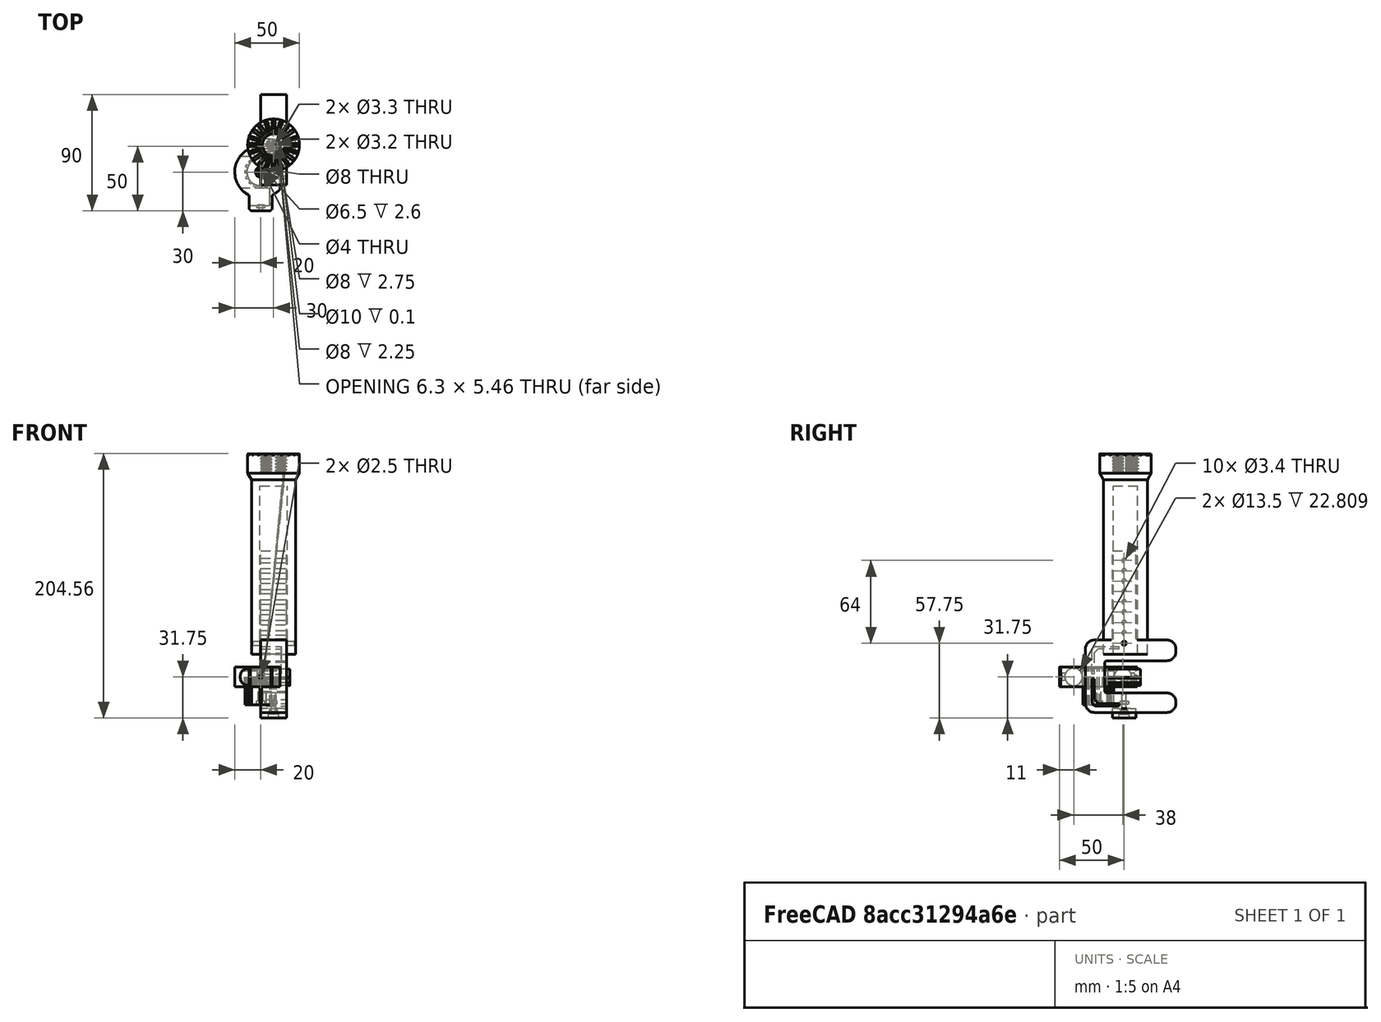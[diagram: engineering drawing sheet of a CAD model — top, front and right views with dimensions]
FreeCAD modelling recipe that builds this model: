
FCSTD DOCUMENT  (FreeCAD 0.18R4 (GitTag))
Label: sop_mic_2
License: All rights reserved
LicenseURL: http://en.wikipedia.org/wiki/All_rights_reserved
objects: Part::Cylinder×59, Part::Cut×55, Part::Box×30, Part::MultiFuse×23, Part::Fillet×12, Part::Prism×8, Mesh::Feature×7, Part::FeaturePython×7, Part::Chamfer×2, Part::Feature×2, App::DocumentObjectGroup×2, Part::Cone×1, Sketcher::SketchObject×1, PartDesign::Pad×1, PartDesign::Body×1, App::FeaturePython×1
note: 203 computed .brp shape members not serialized (recipe doc carries the construction recipe); baked Part::Feature solids carry a one-line shape summary decoded from their .brp

FEATURE [Part::Box] Box  label="Cube"
  AttacherType = Attacher::AttachEngine3D
  Height = 5
  Length = 20
  Width = 30
FEATURE [Part::Cylinder] Cylinder
  Angle = 360
  AttacherType = Attacher::AttachEngine3D
  Height = 10
  Placement = pos=(10,20,-2) rot=(0,0,1;0rad)
  Radius = 1.6
FEATURE [Part::Cut] Cut
  Base = -> Box
  Refine = true
  Tool = -> Cylinder
FEATURE [Part::Prism] Prism
  AttacherType = Attacher::AttachEngine3D
  Circumradius = 3.25
  Height = 10
  Placement = pos=(10,20,9) rot=(1,0,0;3.14159rad)
  Polygon = 6
FEATURE [Part::Cut] Cut001
  Base = -> Cut
  Refine = true
  Tool = -> Prism
FEATURE [Part::Box] Box001  label="Cube001"
  AttacherType = Attacher::AttachEngine3D
  Height = 40
  Length = 20
  Width = 5
FEATURE [Part::Box] Box002  label="Cube002"
  AttacherType = Attacher::AttachEngine3D
  Height = 5
  Length = 20
  Placement = pos=(0,0,35) rot=(0,0,1;0rad)
  Width = 40
FEATURE [Part::Prism] Prism002
  AttacherType = Attacher::AttachEngine3D
  Circumradius = 3.15
  Height = 2.5
  Placement = pos=(0,29,22.5) rot=(1,0,0;1.5708rad)
  Polygon = 6
FEATURE [Part::Cylinder] Cylinder016  label="Cylinder015"
  Angle = 360
  AttacherType = Attacher::AttachEngine3D
  Height = 7.25
  Placement = pos=(0,0,17.5) rot=(1,0,0;1.5708rad)
  Radius = 4
FEATURE [Part::Cylinder] Cylinder013  label="Cylinder012"
  Angle = 360
  AttacherType = Attacher::AttachEngine3D
  Height = 50
  Placement = pos=(0,-16,22.5) rot=(1,0,0;1.5708rad)
  Radius = 1.25
FEATURE [Part::Box] Box004  label="Cube004"
  AttacherType = Attacher::AttachEngine3D
  Height = 10
  Length = 20
  Placement = pos=(-10,0,12.5) rot=(0,0,1;0rad)
  Width = 7.25
FEATURE [Part::Cylinder] Cylinder015  label="Cylinder014"
  Angle = 360
  AttacherType = Attacher::AttachEngine3D
  Height = 7.25
  Placement = pos=(0,0,17.5) rot=(1,0,0;1.5708rad)
  Radius = 9
FEATURE [Part::Cut] Cut013
  Base = -> Cylinder015
  Placement = pos=(0,7.25,0) rot=(0,0,1;0rad)
  Refine = true
  Tool = -> Cylinder016
FEATURE [Part::Cylinder] Cylinder014  label="Cylinder013"
  Angle = 360
  AttacherType = Attacher::AttachEngine3D
  Height = 10
  Placement = pos=(0,-16,22.5) rot=(1,0,0;1.5708rad)
  Radius = 4
FEATURE [Part::MultiFuse] Fusion004
  Placement = pos=(0,57,0) rot=(0,0,1;0rad)
  Refine = true
  Shapes = -> [Cylinder013,Cylinder014]
FEATURE [Part::MultiFuse] Fusion005
  Placement = pos=(0,-26.5,-5) rot=(0,0,1;0rad)
  Refine = true
  Shapes = -> [Prism002,Fusion004]
FEATURE [Part::Cut] Cut012
  Base = -> Box004
  Refine = true
  Tool = -> Fusion005
FEATURE [Part::Fillet] Fillet004
  Base = -> Cut012
  Edges = 1 edges r=3: [Edge15]
FEATURE [Part::Fillet] Fillet005
  Base = -> Fillet004
  Edges = 3 edges r=3: [Edge13,Edge17,Edge20]
FEATURE [Part::MultiFuse] Fusion006
  Refine = true
  Shapes = -> [Cut013,Fillet005]
FEATURE [Part::Fillet] Fillet006  label="tornillos_para_metal"
  Base = -> Fusion006
  Edges = 4 edges r=1: [Edge5,Edge9,Edge12,Edge17]
  Placement = pos=(10,2.5,-2) rot=(-1,0,0;1.5708rad)
FEATURE [Part::Cylinder] Cylinder017  label="Cylinder016"
  Angle = 360
  AttacherType = Attacher::AttachEngine3D
  Height = 7
  Placement = pos=(10,0,-27) rot=(0,0,1;0rad)
  Radius = 12.5
FEATURE [Part::Prism] Prism003
  AttacherType = Attacher::AttachEngine3D
  Circumradius = 3.15
  Height = 3
  Placement = pos=(10,-4e-15,-20) rot=(1,0,0;3.14159rad)
  Polygon = 6
FEATURE [Part::Cut] Cut014
  Base = -> Cylinder017
  Refine = true
  Tool = -> Prism003
FEATURE [Part::Cylinder] Cylinder018  label="Cylinder017"
  Angle = 360
  AttacherType = Attacher::AttachEngine3D
  Height = 2.75
  Placement = pos=(10,0,-27) rot=(0,0,1;0rad)
  Radius = 4
FEATURE [Part::Cut] Cut015
  Base = -> Cut014
  Refine = true
  Tool = -> Cylinder018
FEATURE [Part::Cylinder] Cylinder019  label="Cylinder018"
  Angle = 360
  AttacherType = Attacher::AttachEngine3D
  Height = 22.75
  Placement = pos=(10,0,-31) rot=(0,0,1;0rad)
  Radius = 1.6
FEATURE [Part::Cut] Cut016  label="plato_tornillo"
  Base = -> Cut015
  Placement = pos=(0,20,42) rot=(0,0,1;0rad)
  Refine = true
  Tool = -> Cylinder019
FEATURE [Part::MultiFuse] Fusion
  Refine = true
  Shapes = -> [Cut001,Box001,Box002]
FEATURE [Part::Fillet] Fillet
  Base = -> Fusion
  Edges = 4 edges r=2: [Edge6,Edge14,Edge18,Edge33]
FEATURE [Part::Fillet] Fillet007  label="soporte_escritorio1"
  Base = -> Fillet
  Edges = 1 edges r=2: [Edge50]
FEATURE [Part::Box] Box005  label="Cube005"
  AttacherType = Attacher::AttachEngine3D
  Height = 80
  Length = 20
  Placement = pos=(0,11,40) rot=(0,0,1;0rad)
  Width = 18
FEATURE [Part::MultiFuse] Fusion007  label="soporte_escritorio2"
  Refine = true
  Shapes = -> [Fillet007,Box005]
FEATURE [Part::Cylinder] Cylinder021  label="Cylinder020"
  Angle = 360
  AttacherType = Attacher::AttachEngine3D
  Height = 140
  Placement = pos=(10,21,40) rot=(0,0,1;0rad)
  Radius = 17
FEATURE [Part::Box] Box006  label="Cube006"
  AttacherType = Attacher::AttachEngine3D
  Height = 130
  Length = 21
  Placement = pos=(-0.5,11.5,40) rot=(0,0,1;0rad)
  Width = 19
FEATURE [Part::Cut] Cut017  label="intermedio1"
  Base = -> Cylinder021
  Refine = true
  Tool = -> Box006
FEATURE [Part::Cylinder] Cylinder022  label="tornillo001"
  Angle = 360
  AttacherType = Attacher::AttachEngine3D
  Height = 50
  Placement = pos=(-16,20,48.5) rot=(0,1,0;1.5708rad)
  Radius = 1.7
FEATURE [Part::Cylinder] Cylinder023  label="tornillo002"
  Angle = 360
  AttacherType = Attacher::AttachEngine3D
  Height = 50
  Placement = pos=(-16,20,48.5) rot=(0,1,0;1.5708rad)
  Radius = 1.7
FEATURE [Part::Cut] Cut018  label="intermedio_partial"
  Base = -> Cut017
  Refine = true
  Tool = -> Cylinder022
FEATURE [Part::Cylinder] Cylinder024  label="tornillo003"
  Angle = 360
  AttacherType = Attacher::AttachEngine3D
  Height = 50
  Placement = pos=(-16,20,56.5) rot=(0,1,0;1.5708rad)
  Radius = 1.7
FEATURE [Part::Cylinder] Cylinder025  label="tornillo004"
  Angle = 360
  AttacherType = Attacher::AttachEngine3D
  Height = 50
  Placement = pos=(-16,20,64.5) rot=(0,1,0;1.5708rad)
  Radius = 1.7
FEATURE [Part::Cylinder] Cylinder026  label="tornillo005"
  Angle = 360
  AttacherType = Attacher::AttachEngine3D
  Height = 50
  Placement = pos=(-16,20,72.5) rot=(0,1,0;1.5708rad)
  Radius = 1.7
FEATURE [Part::Cylinder] Cylinder027  label="tornillo006"
  Angle = 360
  AttacherType = Attacher::AttachEngine3D
  Height = 50
  Placement = pos=(-16,20,80.5) rot=(0,1,0;1.5708rad)
  Radius = 1.7
FEATURE [Part::Cylinder] Cylinder028  label="tornillo007"
  Angle = 360
  AttacherType = Attacher::AttachEngine3D
  Height = 50
  Placement = pos=(-16,20,88.5) rot=(0,1,0;1.5708rad)
  Radius = 1.7
FEATURE [Part::Cylinder] Cylinder029  label="tornillo008"
  Angle = 360
  AttacherType = Attacher::AttachEngine3D
  Height = 50
  Placement = pos=(-16,20,96.5) rot=(0,1,0;1.5708rad)
  Radius = 1.7
FEATURE [Part::Cylinder] Cylinder030  label="tornillo009"
  Angle = 360
  AttacherType = Attacher::AttachEngine3D
  Height = 50
  Placement = pos=(-16,20,104.5) rot=(0,1,0;1.5708rad)
  Radius = 1.7
FEATURE [Part::Cylinder] Cylinder031  label="tornillo010"
  Angle = 360
  AttacherType = Attacher::AttachEngine3D
  Height = 50
  Placement = pos=(-16,20,112.5) rot=(0,1,0;1.5708rad)
  Radius = 1.7
FEATURE [Part::MultiFuse] Fusion008
  Refine = true
  Shapes = -> [Cylinder023,Cylinder024,Cylinder025,Cylinder026,Cylinder027,Cylinder028,Cylinder029,Cylinder031,Cylinder030]
FEATURE [Part::Cut] Cut019  label="soporte_escritorio_v2"
  Base = -> Fusion007
  Refine = true
  Tool = -> Fusion008
FEATURE [Mesh::Feature] Mesh  label="tornillos_para_metal (Meshed)"
FEATURE [Mesh::Feature] Mesh001  label="plato_tornillo_gordo_old (Meshed)"
FEATURE [Part::Cylinder] Cylinder032
  Angle = 360
  AttacherType = Attacher::AttachEngine3D
  Height = 10
  Placement = pos=(10,20,-2) rot=(0,0,1;0rad)
  Radius = 1.6
FEATURE [Part::Cylinder] Cylinder033
  Angle = 360
  AttacherType = Attacher::AttachEngine3D
  Height = 1.2
  Placement = pos=(10,20,-2) rot=(0,0,1;0rad)
  Radius = 5
FEATURE [Part::Cut] Cut020
  Base = -> Cylinder033
  Placement = pos=(0,0,5.8) rot=(0,0,1;0rad)
  Refine = true
  Tool = -> Cylinder032
FEATURE [Part::MultiFuse] Fusion009  label="soporte_escritorio_x"
  Refine = true
  Shapes = -> [Cut019,Cut020]
FEATURE [Part::Prism] Prism005
  AttacherType = Attacher::AttachEngine3D
  Circumradius = 3.25
  Height = 10
  Placement = pos=(10,20,12) rot=(1,0,0;3.14159rad)
  Polygon = 6
FEATURE [Part::Cut] Cut021
  Base = -> Fusion009
  Refine = true
  Tool = -> Prism005
FEATURE [Part::Cylinder] Cylinder034
  Angle = 360
  AttacherType = Attacher::AttachEngine3D
  Height = 1.5
  Placement = pos=(10,20,0) rot=(0,0,1;0rad)
  Radius = 4.6
FEATURE [Part::Cylinder] Cylinder035
  Angle = 360
  AttacherType = Attacher::AttachEngine3D
  Height = 10
  Placement = pos=(10,20,-2) rot=(0,0,1;0rad)
  Radius = 1.6
FEATURE [Part::Cut] Cut022
  Base = -> Cylinder034
  Refine = true
  Tool = -> Cylinder035
FEATURE [Part::MultiFuse] Fusion010  label="soporte_escritorio_y"
  Refine = true
  Shapes = -> [Cut022,Cut021]
FEATURE [Part::Prism] Prism006
  AttacherType = Attacher::AttachEngine3D
  Circumradius = 3.25
  Height = 2.3
  Placement = pos=(10,20,-28) rot=(1,0,0;3.14159rad)
  Polygon = 6
FEATURE [Part::Box] Box007  label="Cube007"
  AttacherType = Attacher::AttachEngine3D
  Height = 2.3
  Length = 6.5
  Placement = pos=(6.75,17.18,-30.3) rot=(0,0,1;0rad)
  Width = 2.82
FEATURE [Part::MultiFuse] Fusion011
  Placement = pos=(30,10,31.8) rot=(0,0,1;1.5708rad)
  Refine = true
  Shapes = -> [Prism006,Box007]
FEATURE [Part::Cylinder] Cylinder038
  Angle = 360
  AttacherType = Attacher::AttachEngine3D
  Height = 5
  Placement = pos=(10,20,0) rot=(0,0,1;0rad)
  Radius = 4.6
FEATURE [Part::Cylinder] Cylinder039
  Angle = 360
  AttacherType = Attacher::AttachEngine3D
  Height = 10
  Placement = pos=(10,20,-2) rot=(0,0,1;0rad)
  Radius = 1.6
FEATURE [Part::Cut] Cut025
  Base = -> Cylinder038
  Refine = true
  Tool = -> Cylinder039
FEATURE [Part::MultiFuse] Fusion012
  Refine = true
  Shapes = -> [Cut025,Fusion010]
FEATURE [Part::Cut] Cut026  label="soporte_escritorio"
  Base = -> Fusion012
  Refine = true
  Tool = -> Fusion011
FEATURE [Part::Cylinder] Cylinder003
  Angle = 360
  AttacherType = Attacher::AttachEngine3D
  Height = 23
  Radius = 11
FEATURE [Part::Box] Box009  label="Cube009"
  AttacherType = Attacher::AttachEngine3D
  Height = 5
  Length = 25
  Placement = pos=(14,-5,0) rot=(0,0,1;0rad)
  Width = 10
FEATURE [Part::Cylinder] Cylinder042
  Angle = 360
  AttacherType = Attacher::AttachEngine3D
  Height = 22
  Placement = pos=(0,0,15) rot=(0,1,0;1.5708rad)
  Radius = 1.1
FEATURE [Part::FeaturePython] Array  # Draft array (typed FeaturePython)
  Angle = 360
  ArrayType = 1
  Axis = (0,0,1)
  Base = -> Cylinder042
  Center = (0,0,0)
  Fuse = false
  IntervalAxis = (0,0,0)
  IntervalX = (1,0,0)
  IntervalY = (0,1,0)
  IntervalZ = (0,0,1)
  NumberPolar = 10
  NumberX = 2
  NumberY = 2
  NumberZ = 1
FEATURE [Part::Cut] Cut029
  Base = -> Array
  Refine = true
  Tool = -> Cylinder003
FEATURE [Part::Cylinder] Cylinder043
  Angle = 360
  AttacherType = Attacher::AttachEngine3D
  Height = 15
  Radius = 20
FEATURE [Part::FeaturePython] ScrewTap  label="M20x40.0-ScrewTap"  # Fasteners workbench fastener (typed FeaturePython)
  Placement = pos=(0,0,15) rot=(0,0,1;0rad)
  baseObject = -> Cylinder043 [Edge1]
  diameter = 14
  invert = false
  length = 40
  matchOuter = false
  offset = 0
  thread = true
FEATURE [Part::Cut] Cut028
  Base = -> Cylinder043
  Refine = true
  Tool = -> ScrewTap
FEATURE [Part::Cut] Cut003
  Base = -> Cut028
  Refine = true
  Tool = -> Cut029
FEATURE [Part::Box] Box010  label="Cube010"
  AttacherType = Attacher::AttachEngine3D
  Height = 5
  Length = 25
  Placement = pos=(-38,-5,0) rot=(0,0,1;0rad)
  Width = 10
FEATURE [Part::MultiFuse] Fusion014
  Refine = true
  Shapes = -> [Box010,Box009,Cut003]
FEATURE [Part::Fillet] Fillet008
  Base = -> Fusion014
  Edges = 7 edges r=3: [Edge6,Edge9,Edge11,Edge42,Edge43,Edge46,Edge47]
FEATURE [Part::Fillet] Fillet001
  Base = -> Fillet008
  Edges = 1 edges r=2: [Edge24]
FEATURE [Part::Fillet] Fillet002  label="final_part_soporte_superior_estante"
  Base = -> Fillet001
  Edges = 3 edges r=2: [Edge27,Edge71,Edge74]
FEATURE [Part::Cylinder] Cylinder044
  Angle = 360
  AttacherType = Attacher::AttachEngine3D
  Height = 20
  Radius = 40
FEATURE [Part::Cylinder] Cylinder045
  Angle = 360
  AttacherType = Attacher::AttachEngine3D
  Height = 20
  Radius = 20
FEATURE [Part::Cut] Cut030
  Base = -> Cylinder044
  Refine = true
  Tool = -> Cylinder045
FEATURE [Part::Cut] Cut031
  Base = -> Fillet002
  Refine = true
  Tool = -> Cut030
FEATURE [Part::Cylinder] Cylinder046
  Angle = 360
  AttacherType = Attacher::AttachEngine3D
  Height = 22
  Placement = pos=(0,0,15) rot=(0,1,0;1.5708rad)
  Radius = 1.1
FEATURE [Part::FeaturePython] Array001  # Draft array (typed FeaturePython)
  Angle = 360
  ArrayType = 1
  Axis = (0,0,1)
  Base = -> Cylinder046
  Center = (0,0,0)
  Fuse = false
  IntervalAxis = (0,0,0)
  IntervalX = (1,0,0)
  IntervalY = (0,1,0)
  IntervalZ = (0,0,1)
  NumberPolar = 10
  NumberX = 2
  NumberY = 2
  NumberZ = 1
  Placement = pos=(0,0,0) rot=(0,0,1;0.314159rad)
FEATURE [Part::Cylinder] Cylinder047
  Angle = 360
  AttacherType = Attacher::AttachEngine3D
  Height = 50
  Radius = 11
FEATURE [Part::Cut] Cut032
  Base = -> Array001
  Refine = true
  Tool = -> Cylinder047
FEATURE [Part::Cut] Cut033
  Base = -> Cut031
  Placement = pos=(10,21,180) rot=(0,0,1;0rad)
  Refine = true
  Tool = -> Cut032
FEATURE [Part::MultiFuse] Fusion015
  Refine = true
  Shapes = -> [Cut033,Cut018]
FEATURE [Part::Cone] Cone
  Angle = 360
  AttacherType = Attacher::AttachEngine3D
  Height = 5.2
  Radius1 = 17
  Radius2 = 20
FEATURE [Part::Cylinder] Cylinder048
  Angle = 360
  AttacherType = Attacher::AttachEngine3D
  Height = 10
  Radius = 17
FEATURE [Part::Cut] Cut034
  Base = -> Cone
  Placement = pos=(10,21,174.8) rot=(0,0,1;0rad)
  Refine = true
  Tool = -> Cylinder048
FEATURE [Part::MultiFuse] Fusion016  label="soporte_vertical_escritorio"
  Refine = true
  Shapes = -> [Fusion015,Cut034]
FEATURE [Mesh::Feature] Mesh003  label="soporte_vertical_escritorio (Meshed)"
FEATURE [Part::Cylinder] Cylinder011  label="Cylinder010"
  Angle = 360
  AttacherType = Attacher::AttachEngine3D
  Height = 50
  Placement = pos=(0,-16,22.5) rot=(1,0,0;1.5708rad)
  Radius = 1.25
FEATURE [Part::Cylinder] Cylinder012  label="Cylinder011"
  Angle = 360
  AttacherType = Attacher::AttachEngine3D
  Height = 50
  Placement = pos=(0,69,22.5) rot=(1,0,0;1.5708rad)
  Radius = 1.25
FEATURE [Part::Prism] Prism008
  AttacherType = Attacher::AttachEngine3D
  Circumradius = 3.15
  Height = 2.4
  Placement = pos=(0,28,22.5) rot=(1,0,0;1.5708rad)
  Polygon = 6
FEATURE [Part::Prism] Prism001
  AttacherType = Attacher::AttachEngine3D
  Circumradius = 3.15
  Height = 2.4
  Placement = pos=(0,-25.5,22.5) rot=(1,0,0;1.5708rad)
  Polygon = 6
FEATURE [Part::Cylinder] Cylinder051  label="Cylinder049"
  Angle = 360
  AttacherType = Attacher::AttachEngine3D
  Height = 50
  Placement = pos=(0,69,22.5) rot=(1,0,0;1.5708rad)
  Radius = 1.25
FEATURE [Part::Box] Box011  label="Cube011"
  AttacherType = Attacher::AttachEngine3D
  Height = 15
  Length = 16
  Placement = pos=(-8,29,15) rot=(0,0,1;0rad)
  Width = 1
FEATURE [Part::Cut] Cut037
  Base = -> Box011
  Refine = true
  Tool = -> Cylinder051
FEATURE [Part::Box] Box012  label="Cube012"
  AttacherType = Attacher::AttachEngine3D
  Height = 15
  Length = 16
  Placement = pos=(-8,29,15) rot=(0,0,1;0rad)
  Width = 1
FEATURE [Part::Cylinder] Cylinder052  label="Cylinder021"
  Angle = 360
  AttacherType = Attacher::AttachEngine3D
  Height = 50
  Placement = pos=(0,69,22.5) rot=(1,0,0;1.5708rad)
  Radius = 1.25
FEATURE [Part::Cut] Cut038
  Base = -> Box012
  Placement = pos=(0,-59,0) rot=(0,0,1;0rad)
  Refine = true
  Tool = -> Cylinder052
FEATURE [Part::Cylinder] Cylinder002
  Angle = 360
  AttacherType = Attacher::AttachEngine3D
  Height = 19.75
  Placement = pos=(0,0,15) rot=(0,1,0;1.5708rad)
  Radius = 0.9
FEATURE [Part::FeaturePython] Array002  # Draft array (typed FeaturePython)
  Angle = 360
  ArrayType = 1
  Axis = (0,0,1)
  Base = -> Cylinder002
  Center = (0,0,0)
  Fuse = false
  IntervalAxis = (0,0,0)
  IntervalX = (1,0,0)
  IntervalY = (0,1,0)
  IntervalZ = (0,0,1)
  NumberPolar = 10
  NumberX = 2
  NumberY = 2
  NumberZ = 1
FEATURE [Part::Cylinder] Cylinder004
  Angle = 360
  AttacherType = Attacher::AttachEngine3D
  Height = 23
  Radius = 11.2
FEATURE [Part::Cut] Cut002  label="aspas"
  Base = -> Array002
  Refine = true
  Tool = -> Cylinder004
FEATURE [Part::Cylinder] Cylinder006
  Angle = 360
  AttacherType = Attacher::AttachEngine3D
  Height = 32
  Radius = 10.5
FEATURE [Part::Cylinder] Cylinder005
  Angle = 360
  AttacherType = Attacher::AttachEngine3D
  Height = 15
  Placement = pos=(0,0,15) rot=(0,0,1;0rad)
  Radius = 20
FEATURE [Part::Cut] Cut004
  Base = -> Cylinder005
  Refine = true
  Tool = -> Cylinder006
FEATURE [Part::MultiFuse] Fusion001
  Refine = true
  Shapes = -> [Cut004,Cut002]
FEATURE [Part::Cylinder] Cylinder007
  Angle = 360
  AttacherType = Attacher::AttachEngine3D
  Height = 50
  Placement = pos=(-24,19,22.5) rot=(0,1,0;1.5708rad)
  Radius = 6.75
FEATURE [Part::Box] Box013  label="Cube013"
  AttacherType = Attacher::AttachEngine3D
  Height = 15
  Length = 18
  Placement = pos=(-9,-29,15) rot=(0,0,1;0rad)
  Width = 18
FEATURE [Part::Box] Box003  label="Cube003"
  AttacherType = Attacher::AttachEngine3D
  Height = 15
  Length = 18
  Placement = pos=(-9,11,15) rot=(0,0,1;0rad)
  Width = 18
FEATURE [Part::MultiFuse] Fusion002
  Refine = true
  Shapes = -> [Fusion001,Box013,Box003]
FEATURE [Part::Cylinder] Cylinder008
  Angle = 360
  AttacherType = Attacher::AttachEngine3D
  Height = 50
  Placement = pos=(-24,-19,22.5) rot=(0,1,0;1.5708rad)
  Radius = 6.75
FEATURE [Part::Cut] Cut005
  Base = -> Fusion002
  Refine = true
  Tool = -> Cylinder008
FEATURE [Part::Cut] Cut006
  Base = -> Cut005
  Refine = true
  Tool = -> Cylinder007
FEATURE [Part::Fillet] Fillet003  label="part_soporte_inferior_estante"
  Base = -> Cut006
  Edges = 12 edges r=1: [Edge2,Edge5,Edge7,Edge19,Edge21,Edge74,Edge75,Edge76,Edge77,Edge79,Edge80,Edge83]
FEATURE [Part::Cut] Cut008
  Base = -> Fillet003
  Refine = true
  Tool = -> Cylinder011
FEATURE [Part::Cut] Cut009
  Base = -> Cut008
  Refine = true
  Tool = -> Cylinder012
FEATURE [Part::Cut] Cut035
  Base = -> Cut009
  Refine = true
  Tool = -> Prism001
FEATURE [Part::Cut] Cut036  label="final_soporte_inferior_estante11"
  Base = -> Cut035
  Refine = true
  Tool = -> Prism008
FEATURE [Part::MultiFuse] Fusion017
  Refine = true
  Shapes = -> [Cut038,Cut036,Cut037]
FEATURE [Part::Fillet] Fillet010  label="final_soporte_inferior_estante1"
  Base = -> Fusion017
  Edges = 4 edges r=0.9: [Edge1,Edge6,Edge99,Edge102]
FEATURE [Sketcher::SketchObject] CopySketch
  Placement = pos=(0,0,15) rot=(1,0,0;3.14159rad)
  sketch-geometry (8):
    g0: LineSegment StartX=9 StartY=28 StartZ=0 EndX=9 EndY=18.4662 EndZ=0
    g1: ArcOfCircle CenterX=10 CenterY=18.4662 CenterZ=0 NormalX=0 NormalY=0 NormalZ=1 AngleXU=0 Radius=1 StartAngle=3.14159 EndAngle=4.21607
    g2: ArcOfCircle CenterX=10 CenterY=-18.4662 CenterZ=0 NormalX=0 NormalY=0 NormalZ=1 AngleXU=0 Radius=1 StartAngle=2.06711 EndAngle=3.14159
    g3: LineSegment StartX=9 StartY=-18.4662 StartZ=0 EndX=9 EndY=-28 EndZ=0
    g4: ArcOfCircle CenterX=0 CenterY=0 CenterZ=0 NormalX=0 NormalY=0 NormalZ=1 AngleXU=0 Radius=20 StartAngle=5.20871 EndAngle=7.35766
    g5: LineSegment StartX=9 StartY=28 StartZ=0 EndX=27.4743 EndY=28 EndZ=0
    g6: LineSegment StartX=27.4743 StartY=28 StartZ=0 EndX=27.4743 EndY=-28 EndZ=0
    g7: LineSegment StartX=27.4743 StartY=-28 StartZ=0 EndX=9 EndY=-28 EndZ=0
  constraints (12):
    c: Tangent(g0,g1) = -1.5708
    c: Tangent(g3,g2) = -1.5708
    c: Coincident(g4,g-1)
    c: Coincident(g4,g1)
    c: Coincident(g4,g2)
    c: Coincident(g0,g5)
    c: Horizontal(g5)
    c: Coincident(g5,g6)
    c: Vertical(g6)
    c: Coincident(g6,g7)
    c: Coincident(g7,g3)
    c: Horizontal(g7)
FEATURE [PartDesign::Pad] Pad
  Length = 50
  Length2 = 100
  Placement = pos=(0,0,15) rot=(1,0,0;3.14159rad)
  Profile = -> CopySketch
  Type = 0
FEATURE [PartDesign::Body] Body
  Group = -> [Pad]
  Origin = -> Origin
  Placement = pos=(0,0,25) rot=(0,0,1;0rad)
  Tip = -> Pad
FEATURE [Part::Box] Box014  label="Cube014"
  AttacherType = Attacher::AttachEngine3D
  Height = 15
  Length = 10
  Placement = pos=(7,-27,15) rot=(0,0,1;0rad)
  Width = 54
FEATURE [Part::Cut] Cut039
  Base = -> Box014
  Tool = -> Body
FEATURE [Part::Cylinder] Cylinder053  label="Cylinder050"
  Angle = 360
  AttacherType = Attacher::AttachEngine3D
  Height = 15
  Placement = pos=(0,0,15) rot=(0,0,1;0rad)
  Radius = 10.5
FEATURE [Part::MultiFuse] Fusion018
  Shapes = -> [Cut039,Cylinder053]
FEATURE [Part::MultiFuse] Fusion019
  Shapes = -> [Fusion018,Fillet010]
FEATURE [Part::Box] Box015  label="Cube015"
  AttacherType = Attacher::AttachEngine3D
  Height = 15
  Length = 14
  Placement = pos=(15,-27,15) rot=(0,0,1;0rad)
  Width = 54
FEATURE [Part::Box] Box016  label="Cube016"
  AttacherType = Attacher::AttachEngine3D
  Height = 10
  Length = 40
  Placement = pos=(-20,-20,5) rot=(0,0,1;0rad)
  Width = 40
FEATURE [Part::Cut] Cut040
  Base = -> Fusion019
  Tool = -> Box016
FEATURE [Part::Cut] Cut041
  Base = -> Cut040
  Tool = -> Box015
FEATURE [Part::Fillet] Fillet011  label="extremo_microfono_sin_agujero"
  Base = -> Cut041
  Edges = 6 edges r=2: [Edge46,Edge48,Edge49,Edge57,Edge58,Edge59]
FEATURE [Part::Cylinder] Cylinder055  label="base_para_rosca_microfono"
  Angle = 360
  AttacherType = Attacher::AttachEngine3D
  Height = 14
  Radius = 10.5
FEATURE [Part::Cylinder] Cylinder056  label="cortador_base_para_rosca_microfono001"
  Angle = 360
  AttacherType = Attacher::AttachEngine3D
  Height = 14.2
  Placement = pos=(0,0,15) rot=(0,0,1;0rad)
  Radius = 10.8
FEATURE [Part::Box] Box018  label="Cube018"
  AttacherType = Attacher::AttachEngine3D
  Height = 14.2
  Length = 6.3
  Placement = pos=(6,-0.9,15) rot=(0,0,1;0rad)
  Width = 1.8
FEATURE [Part::FeaturePython] Array003  # Draft array (typed FeaturePython)
  Angle = 360
  ArrayType = 1
  Axis = (0,0,1)
  Base = -> Box018
  Center = (0,0,0)
  Fuse = false
  IntervalAxis = (0,0,0)
  IntervalX = (1,0,0)
  IntervalY = (0,1,0)
  IntervalZ = (0,0,1)
  NumberPolar = 16
  NumberX = 2
  NumberY = 2
  NumberZ = 1
FEATURE [Part::MultiFuse] Fusion020
  Shapes = -> [Cylinder056,Array003]
FEATURE [Part::Cut] Cut042  label="extremo_microfono"
  Base = -> Fillet011
  Tool = -> Fusion020
FEATURE [Part::Box] Box019  label="Cube019"
  AttacherType = Attacher::AttachEngine3D
  Height = 14
  Length = 6
  Placement = pos=(6,-0.75,0) rot=(0,0,1;0rad)
  Width = 1.5
FEATURE [Part::FeaturePython] Array004  # Draft array (typed FeaturePython)
  Angle = 360
  ArrayType = 1
  Axis = (0,0,1)
  Base = -> Box019
  Center = (0,0,0)
  Fuse = false
  IntervalAxis = (0,0,0)
  IntervalX = (1,0,0)
  IntervalY = (0,1,0)
  IntervalZ = (0,0,1)
  NumberPolar = 8
  NumberX = 2
  NumberY = 2
  NumberZ = 1
FEATURE [Part::MultiFuse] Fusion021  label="base_para_rosca_microfono001"
  Placement = pos=(0,0,1) rot=(0,0,1;0rad)
  Shapes = -> [Cylinder055,Array004]
FEATURE [Part::Cylinder] Cylinder057  label="Cylinder052"
  Angle = 360
  AttacherType = Attacher::AttachEngine3D
  Height = 13
  Placement = pos=(0,0,3.6) rot=(0,0,1;0rad)
  Radius = 2
FEATURE [Part::Cylinder] Cylinder059  label="Cylinder054"
  Angle = 360
  AttacherType = Attacher::AttachEngine3D
  Height = 2.6
  Placement = pos=(0,0,1) rot=(0,0,1;0rad)
  Radius = 3.25
FEATURE [Part::Cut] Cut043
  Base = -> Fusion021
  Refine = true
  Tool = -> Cylinder059
FEATURE [Part::Cut] Cut044  label="base_para_rosca_microfono_final"
  Base = -> Cut043
  Refine = true
  Tool = -> Cylinder057
FEATURE [Mesh::Feature] Mesh005  label="base_para_rosca_microfono_final (Meshed)"
FEATURE [Part::Cylinder] Cylinder060  label="Cylinder055"
  Angle = 360
  AttacherType = Attacher::AttachEngine3D
  Height = 10
  Placement = pos=(0,0,21.7) rot=(0,0,1;0rad)
  Radius = 4
FEATURE [Part::Cut] Cut045  label="extremo_microfono_done"
  Base = -> Cut042
  Refine = true
  Tool = -> Cylinder060
FEATURE [Mesh::Feature] Mesh006  label="extremo_microfono_done (Meshed)"
FEATURE [Part::Box] Box020  label="Cube020"
  AttacherType = Attacher::AttachEngine3D
  Height = 15
  Length = 20
  Placement = pos=(0,0,-5) rot=(0,0,1;0rad)
  Width = 15
FEATURE [Part::Box] Box021  label="Cube021"
  AttacherType = Attacher::AttachEngine3D
  Height = 16
  Length = 20
  Placement = pos=(0,0,35) rot=(0,0,1;0rad)
  Width = 60
FEATURE [Part::Box] Box022  label="Cube022"
  AttacherType = Attacher::AttachEngine3D
  Height = 56
  Length = 20
  Placement = pos=(0,-10,-5) rot=(0,0,1;0rad)
  Width = 15
FEATURE [Part::Cylinder] Cylinder061
  Angle = 360
  AttacherType = Attacher::AttachEngine3D
  Height = 25
  Placement = pos=(10,20,-9) rot=(0,0,1;0rad)
  Radius = 1.65
FEATURE [Part::Box] Box023  label="Cube023"
  AttacherType = Attacher::AttachEngine3D
  Height = 15
  Length = 20
  Placement = pos=(0,45,-5) rot=(0,0,1;0rad)
  Width = 15
FEATURE [Part::Box] Box024  label="Cube024"
  AttacherType = Attacher::AttachEngine3D
  Height = 15
  Length = 20
  Placement = pos=(0,25,-5) rot=(0,0,1;0rad)
  Width = 26
FEATURE [Part::Box] Box025  label="Cube025"
  AttacherType = Attacher::AttachEngine3D
  Height = 5
  Length = 20
  Placement = pos=(0,8,-5) rot=(0,0,1;0rad)
  Width = 26
FEATURE [Part::Box] Box026  label="Cube026"
  AttacherType = Attacher::AttachEngine3D
  Height = 5
  Length = 20
  Placement = pos=(0,8,5) rot=(0,0,1;0rad)
  Width = 26
FEATURE [Part::MultiFuse] Fusion022
  Refine = true
  Shapes = -> [Box020,Box024,Box022,Box025,Box021,Box023,Box026]
FEATURE [Part::MultiFuse] Fusion023
  Refine = true
  Shapes = -> [Cut026,Fusion022]
FEATURE [Part::Cut] Cut046
  Base = -> Fusion023
  Refine = true
  Tool = -> Cylinder061
FEATURE [Part::Fillet] Fillet012
  Base = -> Cut046
  Edges = 6 edges r=7: [Edge1,Edge3,Edge49,Edge50,Edge51,Edge53]
FEATURE [Part::Chamfer] Chamfer  label="soporte_escritorio_reforzado"
  Base = -> Fillet012
  Edges = 4 edges r=1: [Edge57,Edge58,Edge62,Edge69]
FEATURE [Part::Feature] Body003  label="angulo003"
  Placement = pos=(4,12,36) rot=(0,0,1;1.5708rad)
  shape: bbox 16 x 21 x 21 mm, 10 faces (baked)
FEATURE [Part::Feature] Body004  label="angulo004"
  Placement = pos=(0,31,29) rot=(0.57735,-0.57735,-0.57735;4.18879rad)
  shape: bbox 16 x 21 x 21 mm, 10 faces (baked)
FEATURE [Part::Cut] Cut047
  Base = -> Chamfer
  Refine = true
  Tool = -> Body003
FEATURE [Part::Cut] Cut048  label="soporte_escritorio_super_reforzado"
  Base = -> Cut047
  Refine = true
  Tool = -> Body004
FEATURE [Mesh::Feature] Mesh007  label="soporte_escritorio_super_reforzado (Meshed)"
FEATURE [Part::Cylinder] Cylinder062
  Angle = 360
  AttacherType = Attacher::AttachEngine3D
  Height = 2.75
  Placement = pos=(10,20,15.2) rot=(0,0,1;0rad)
  Radius = 4
FEATURE [Part::Cut] Cut049
  Base = -> Cut016
  Refine = true
  Tool = -> Cylinder062
FEATURE [Part::Box] Box027  label="Cube027"
  AttacherType = Attacher::AttachEngine3D
  Height = 0.7
  Length = 40
  Placement = pos=(-10,0,15) rot=(0,0,1;0rad)
  Width = 50
FEATURE [Part::Cut] Cut050  label="plato_tornillo001"
  Base = -> Cut049
  Refine = true
  Tool = -> Box027
FEATURE [Part::Cylinder] Cylinder063  label="Cylinder065"
  Angle = 360
  AttacherType = Attacher::AttachEngine3D
  Height = 2.75
  Placement = pos=(10,0,-27) rot=(0,0,1;0rad)
  Radius = 4
FEATURE [Part::Prism] Prism009
  AttacherType = Attacher::AttachEngine3D
  Circumradius = 3.15
  Height = 3
  Placement = pos=(10,-4e-15,-20) rot=(1,0,0;3.14159rad)
  Polygon = 6
FEATURE [Part::Cylinder] Cylinder064  label="Cylinder063"
  Angle = 360
  AttacherType = Attacher::AttachEngine3D
  Height = 22.75
  Placement = pos=(10,0,-31) rot=(0,0,1;0rad)
  Radius = 1.6
FEATURE [Part::Cylinder] Cylinder065  label="Cylinder066"
  Angle = 360
  AttacherType = Attacher::AttachEngine3D
  Height = 7
  Placement = pos=(10,0,-27) rot=(0,0,1;0rad)
  Radius = 12.5
FEATURE [Part::Cut] Cut051
  Base = -> Cylinder065
  Refine = true
  Tool = -> Prism009
FEATURE [Part::Cut] Cut052
  Base = -> Cut051
  Refine = true
  Tool = -> Cylinder063
FEATURE [Part::Cut] Cut053  label="plato_tornillo002"
  Base = -> Cut052
  Placement = pos=(0,20,42) rot=(0,0,1;0rad)
  Refine = true
  Tool = -> Cylinder064
FEATURE [Part::Cylinder] Cylinder066  label="Cylinder067"
  Angle = 360
  AttacherType = Attacher::AttachEngine3D
  Height = 2.75
  Placement = pos=(10,20,15.2) rot=(0,0,1;0rad)
  Radius = 4
FEATURE [Part::Cut] Cut055
  Base = -> Cut053
  Refine = true
  Tool = -> Cylinder066
FEATURE [Part::Box] Box028  label="Cube028"
  AttacherType = Attacher::AttachEngine3D
  Height = 0.7
  Length = 40
  Placement = pos=(-10,0,15) rot=(0,0,1;0rad)
  Width = 50
FEATURE [Part::Cut] Cut054  label="plato_tornillo003"
  Base = -> Cut055
  Refine = true
  Tool = -> Box028
FEATURE [Part::Box] Box029  label="Cube029"
  AttacherType = Attacher::AttachEngine3D
  Height = 10
  Length = 40
  Placement = pos=(-10,0,23.5) rot=(0,0,1;0rad)
  Width = 50
FEATURE [Part::Cylinder] Cylinder067  label="Cylinder068"
  Angle = 360
  AttacherType = Attacher::AttachEngine3D
  Height = 7
  Placement = pos=(10,20,21.5) rot=(0,0,1;0rad)
  Radius = 12.5
FEATURE [Part::MultiFuse] Fusion024
  Refine = true
  Shapes = -> [Cut054,Cylinder067]
FEATURE [Part::Box] Box030  label="Cube030"
  AttacherType = Attacher::AttachEngine3D
  Height = 2.3
  Length = 40
  Placement = pos=(-10,0,15.7) rot=(0,0,1;0rad)
  Width = 50
FEATURE [Part::Cut] Cut056
  Base = -> Fusion024
  Refine = true
  Tool = -> Box030
FEATURE [Part::Cut] Cut057
  Base = -> Cut056
  Refine = true
  Tool = -> Box029
FEATURE [Part::Cylinder] Cylinder068  label="Cylinder069"
  Angle = 360
  AttacherType = Attacher::AttachEngine3D
  Height = 7
  Placement = pos=(10,20,21.5) rot=(0,0,1;0rad)
  Radius = 12.5
FEATURE [Part::Cylinder] Cylinder069  label="Cylinder070"
  Angle = 360
  AttacherType = Attacher::AttachEngine3D
  Height = 22.75
  Placement = pos=(10,20,12) rot=(0,0,1;0rad)
  Radius = 1.6
FEATURE [Part::FeaturePython] Point  label="Center"  # WARN: FeaturePython — macro-defined, semantics opaque (R4)
  X = 10
  Y = 20
  Z = 18
FEATURE [App::FeaturePython] Dimension  label="Radius"  # Draft dimension (typed FeaturePython)
  Diameter = false
  Dimline = (10.8,20,18)
  Direction = (0,0,0)
  Distance = 1.6
  End = (10,20,18)
  Normal = (0,0,-1)
  Start = (11.6,20,18)
FEATURE [Part::Cut] Cut058  label="plato_tornillo_fino2"
  Base = -> Cut057
  Refine = true
  Tool = -> Cylinder069
FEATURE [Part::Cylinder] Cylinder070  label="Cylinder071"
  Angle = 360
  AttacherType = Attacher::AttachEngine3D
  Height = 22.75
  Placement = pos=(10,20,21) rot=(0,0,1;0rad)
  Radius = 5
FEATURE [Part::Cut] Cut059
  Base = -> Cut058
  Refine = true
  Tool = -> Cylinder070
FEATURE [Part::Chamfer] Chamfer001  label="plato_tornillo_fino333"
  Base = -> Cut059
  Edges = 1 edges r=2.4: [Edge5]
FEATURE [Part::Box] Box031  label="Cube031"
  AttacherType = Attacher::AttachEngine3D
  Height = 1.4
  Length = 40
  Placement = pos=(-10,0,22.2) rot=(0,0,1;0rad)
  Width = 50
FEATURE [Part::Cut] Cut060  label="plato_tornillo_fino"
  Base = -> Chamfer001
  Refine = true
  Tool = -> Box031
FEATURE [App::DocumentObjectGroup] Group  label="finalizados"
  Group = -> [Fillet006,Fusion016,Cut044,Cut045,Cut048,Cut050,Cut060]
FEATURE [Mesh::Feature] Mesh008  label="plato_tornillo_fino (Meshed)"
FEATURE [App::DocumentObjectGroup] Group001  label="meshes"
  Group = -> [Mesh,Mesh001,Mesh003,Mesh005,Mesh006,Mesh007,Mesh008]
